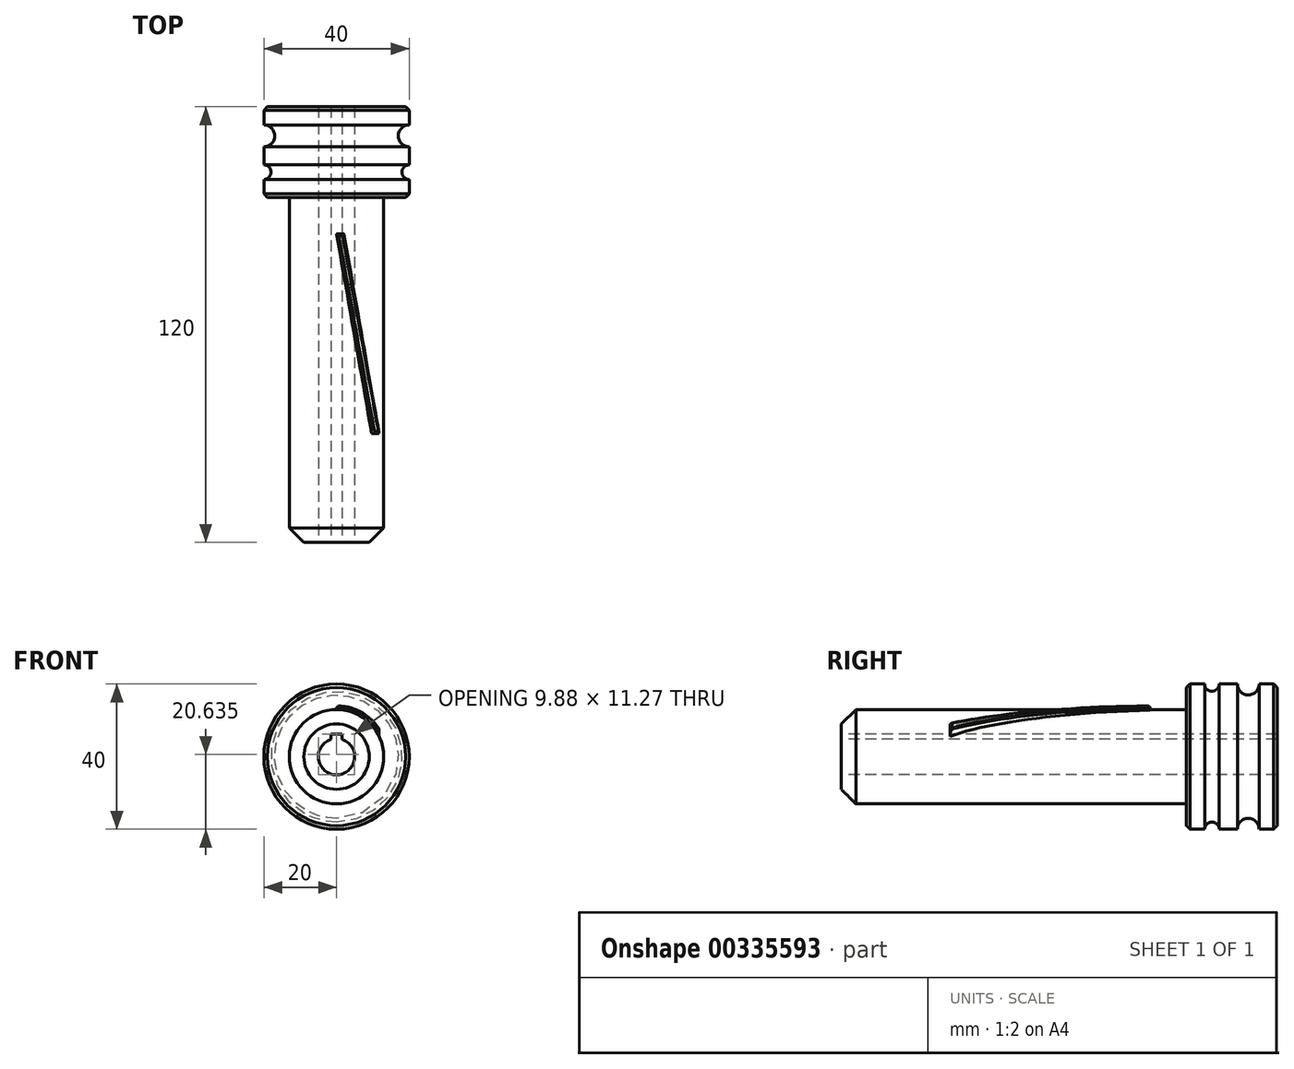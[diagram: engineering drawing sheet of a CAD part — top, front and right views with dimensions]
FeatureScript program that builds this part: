
annotation { "Feature Type Name" : "Feature", "Feature Type Description" : "" }
export const myFeature = defineFeature(function(context is Context, id is Id, definition is map)
    precondition{}
    {
        {
            var Q0;
            Q0=qCreatedBy(makeId("Top.planeOp"),FACE);
            var sketch = newSketch(context, id + "F0", { "sketchPlane" : qUnion([Q0])});
            skLineSegment(sketch, "E0", {"start": v(-20, 70) * mm, "end": v(-20, 45) * mm});
            skLineSegment(sketch, "E1", {"start": v(-20, 45) * mm, "end": v(-13, 45) * mm});
            skLineSegment(sketch, "E2", {"start": v(-13, 45) * mm, "end": v(-13, -50) * mm});
            skLineSegment(sketch, "E3", {"start": v(-13, -50) * mm, "end": v(0, -50) * mm});
            skLineSegment(sketch, "E4", {"start": v(-20, 70) * mm, "end": v(0, 70) * mm});
            skLineSegment(sketch, "E5", {"start": v(0, 68.59) * mm, "end": v(0, -67.14) * mm, "construction": true});
            skLineSegment(sketch, "E6", {"start": v(0, 70) * mm, "end": v(0, -50) * mm});
            skSolve(sketch);
        }
        {
            var Q0;
            Q0 = qSketchRegion(id + "F0", true);
            var Q1;
            Q1=sQuery(id+"F0.wireOp",EDGE,"E6");
            revolve(context, id + "F1", {"entities" : qUnion([Q0]), "axis" : qUnion([Q1]), "revolveType" : RevolveType.FULL});
        }
        {
            var Q0;
            Q0=qCreatedBy(makeId("Top.planeOp"),FACE);
            cPlane(context, id + "F2", {"entities" : qUnion([Q0]), "cplaneType" : CPlaneType.OFFSET, "offset" : 25 * mm, "width" : 150 * mm, "height" : 150 * mm});
        }
        {
            var Q0;
            Q0=qCreatedBy(id+"F2.planeOp",FACE);
            var sketch = newSketch(context, id + "F3", { "sketchPlane" : qUnion([Q0])});
            skLineSegment(sketch, "E7", {"start": v(11.73, -20) * mm, "end": v(2.03, 35) * mm});
            skLineSegment(sketch, "E8.0", {"start": v(9.7, -20) * mm, "end": v(0, 35) * mm});
            skLineSegment(sketch, "E9", {"start": v(2.03, 35) * mm, "end": v(0, 35) * mm});
            skLineSegment(sketch, "E10", {"start": v(11.73, -20) * mm, "end": v(9.7, -20) * mm});
            skSolve(sketch);
        }
        {
            var Q0;
            Q0 = qSketchRegion(id + "F3", true);
            extrude(context, id + "F4", {"entities" : qUnion([Q0]), "operationType" : NewBodyOperationType.ADD, "endBound" : BoundingType.UP_TO_NEXT, "oppositeDirection" : true, "depth" : 25 * mm});
        }
        {
            var Q0;
            Q0=makeQuery(id+"F1.opRevolve","SWEPT_FACE",FACE,{"disambiguationData":[OSD([sQuery(id+"F0.wireOp",EDGE,"E3")])]});
            var sketch = newSketch(context, id + "F5", { "sketchPlane" : qUnion([Q0])});
            skCircle(sketch, "E11.0", {"center": v(0, 0) * mm, "radius": 33 * mm});
            skCircle(sketch, "E12.0", {"center": v(0, 0) * mm, "radius": 14 * mm});
            skSolve(sketch);
        }
        {
            var Q0;
            Q0 = qSketchRegion(id + "F5", true);
            var Q1;
            Q1=makeQuery(id+"F1.opRevolve","SWEPT_FACE",FACE,{"disambiguationData":[OSD([sQuery(id+"F0.wireOp",EDGE,"E1")])]});
            extrude(context, id + "F6", {"entities" : qUnion([Q0]), "operationType" : NewBodyOperationType.REMOVE, "endBound" : BoundingType.UP_TO_SURFACE, "oppositeDirection" : true, "endBoundEntityFace" : qUnion([Q1]), "depth" : 25 * mm});
        }
        {
            var Q0;
            Q0=makeQuery(id+"F6.boolean.opBoolean","INTERSECT",EDGE,{"derivedFrom":[makeQuery(id+"F4.opExtrude","SWEPT_FACE",FACE,{"disambiguationData":[OSD([sQuery(id+"F3.wireOp",EDGE,"E7")])]}),makeQuery(id+"F6.opExtrude","SWEPT_FACE",FACE,{"disambiguationData":[OSD([sQuery(id+"F5.wireOp",EDGE,"E12.0")])]})]});
            var Q1;
            Q1=makeQuery(id+"F6.boolean.opBoolean","INTERSECT",EDGE,{"derivedFrom":[makeQuery(id+"F4.opExtrude","SWEPT_FACE",FACE,{"disambiguationData":[OSD([sQuery(id+"F3.wireOp",EDGE,"E8.0")])]}),makeQuery(id+"F6.opExtrude","SWEPT_FACE",FACE,{"disambiguationData":[OSD([sQuery(id+"F5.wireOp",EDGE,"E12.0")])]})]});
            var Q2;
            Q2=makeQuery(id+"F6.boolean.opBoolean","INTERSECT",EDGE,{"derivedFrom":[makeQuery(id+"F4.opExtrude","SWEPT_FACE",FACE,{"disambiguationData":[OSD([sQuery(id+"F3.wireOp",EDGE,"E10")])]}),makeQuery(id+"F6.opExtrude","SWEPT_FACE",FACE,{"disambiguationData":[OSD([sQuery(id+"F5.wireOp",EDGE,"E12.0")])]})]});
            var Q3;
            Q3=makeQuery(id+"F6.boolean.opBoolean","INTERSECT",EDGE,{"derivedFrom":[makeQuery(id+"F4.opExtrude","SWEPT_FACE",FACE,{"disambiguationData":[OSD([sQuery(id+"F3.wireOp",EDGE,"E9")])]}),makeQuery(id+"F6.opExtrude","SWEPT_FACE",FACE,{"disambiguationData":[OSD([sQuery(id+"F5.wireOp",EDGE,"E12.0")])]})]});
            chamfer(context, id + "F7", {"entities" : qUnion([Q0, Q1, Q2, Q3]), "width" : .5 * mm, "tangentPropagation" : true});
        }
        {
            var Q0;
            Q0=makeQuery(id+"F1.opRevolve","SWEPT_EDGE",EDGE,{"disambiguationData":[OSD([sQuery(id+"F0.wireOp",EDGE,"E2"),sQuery(id+"F0.wireOp",EDGE,"E3")])]});
            chamfer(context, id + "F8", {"entities" : qUnion([Q0]), "width" : 4 * mm, "tangentPropagation" : true});
        }
        {
            var Q0;
            Q0=makeQuery(id+"F1.opRevolve","SWEPT_EDGE",EDGE,{"disambiguationData":[OSD([sQuery(id+"F0.wireOp",EDGE,"E0"),sQuery(id+"F0.wireOp",EDGE,"E4")])]});
            var Q1;
            Q1=makeQuery(id+"F1.opRevolve","SWEPT_EDGE",EDGE,{"disambiguationData":[OSD([sQuery(id+"F0.wireOp",EDGE,"E0"),sQuery(id+"F0.wireOp",EDGE,"E1")])]});
            chamfer(context, id + "F9", {"entities" : qUnion([Q0, Q1]), "width" : 1 * mm, "tangentPropagation" : true});
        }
        {
            var Q0;
            Q0=qCreatedBy(makeId("Top.planeOp"),FACE);
            var sketch = newSketch(context, id + "F10", { "sketchPlane" : qUnion([Q0])});
            skLineSegment(sketch, "E13", {"start": v(0, 80.44) * mm, "end": v(0, -57.1) * mm, "construction": true});
            skSolve(sketch);
        }
        {
            var Q0;
            Q0=qCreatedBy(makeId("Top.planeOp"),FACE);
            var sketch = newSketch(context, id + "F11", { "sketchPlane" : qUnion([Q0])});
            skCircle(sketch, "E14", {"center": v(-20, 62) * mm, "radius": 3 * mm});
            skCircle(sketch, "E15", {"center": v(-20, 52) * mm, "radius": 2 * mm});
            skSolve(sketch);
        }
        {
            var Q0;
            Q0=makeQuery(id+"F11.imprint","IMPRINT",FACE,{"disambiguationData":[TD([[makeQuery(id+"F11.imprint","IMPRINT",EDGE,{"derivedFrom":sQuery(id+"F11.wireOp",EDGE,"E14")}),1.0]])]});
            var Q1;
            Q1=makeQuery(id+"F11.imprint","IMPRINT",FACE,{"disambiguationData":[TD([[makeQuery(id+"F11.imprint","IMPRINT",EDGE,{"derivedFrom":sQuery(id+"F11.wireOp",EDGE,"E15")}),1.0]])]});
            var Q2;
            Q2=sQuery(id+"F10.wireOp",EDGE,"E13");
            revolve(context, id + "F12", {"operationType" : NewBodyOperationType.REMOVE, "entities" : qUnion([Q0, Q1]), "axis" : qUnion([Q2]), "revolveType" : RevolveType.FULL, "oppositeDirection" : true});
        }
        {
            var Q0;
            Q0=makeQuery(id+"F1.opRevolve","SWEPT_EDGE",EDGE,{"disambiguationData":[OSD([sQuery(id+"F0.wireOp",EDGE,"E1"),sQuery(id+"F0.wireOp",EDGE,"E2")])]});
            fillet(context, id + "F13", {"entities" : qUnion([Q0]), "radius" : .5 * mm, "tangentPropagation" : true, "allowEdgeOverflow" : false});
        }
        {
            var Q0;
            Q0=makeQuery(id+"F1.opRevolve","SWEPT_FACE",FACE,{"disambiguationData":[OSD([sQuery(id+"F0.wireOp",EDGE,"E3")])]});
            var sketch = newSketch(context, id + "F14", { "sketchPlane" : qUnion([Q0])});
            skArc(sketch, "E16", {"start": v(-1.5, 4.77) * mm, "mid": v(0, -5) * mm, "end": v(1.5, 4.77) * mm});
            skLineSegment(sketch, "E17.top", {"start": v(-1.5, 6.27) * mm, "end": v(1.5, 6.27) * mm});
            skLineSegment(sketch, "E17.left", {"start": v(-1.5, 4.77) * mm, "end": v(-1.5, 6.27) * mm});
            skLineSegment(sketch, "E17.right", {"start": v(1.5, 4.77) * mm, "end": v(1.5, 6.27) * mm});
            skLineSegment(sketch, "E18", {"start": v(0, 0) * mm, "end": v(0, 6.27) * mm, "construction": true});
            skSolve(sketch);
        }
        {
            var Q0;
            Q0 = qSketchRegion(id + "F14", true);
            extrude(context, id + "F15", {"entities" : qUnion([Q0]), "operationType" : NewBodyOperationType.REMOVE, "endBound" : BoundingType.THROUGH_ALL, "oppositeDirection" : true, "depth" : 25 * mm});
        }
    });
